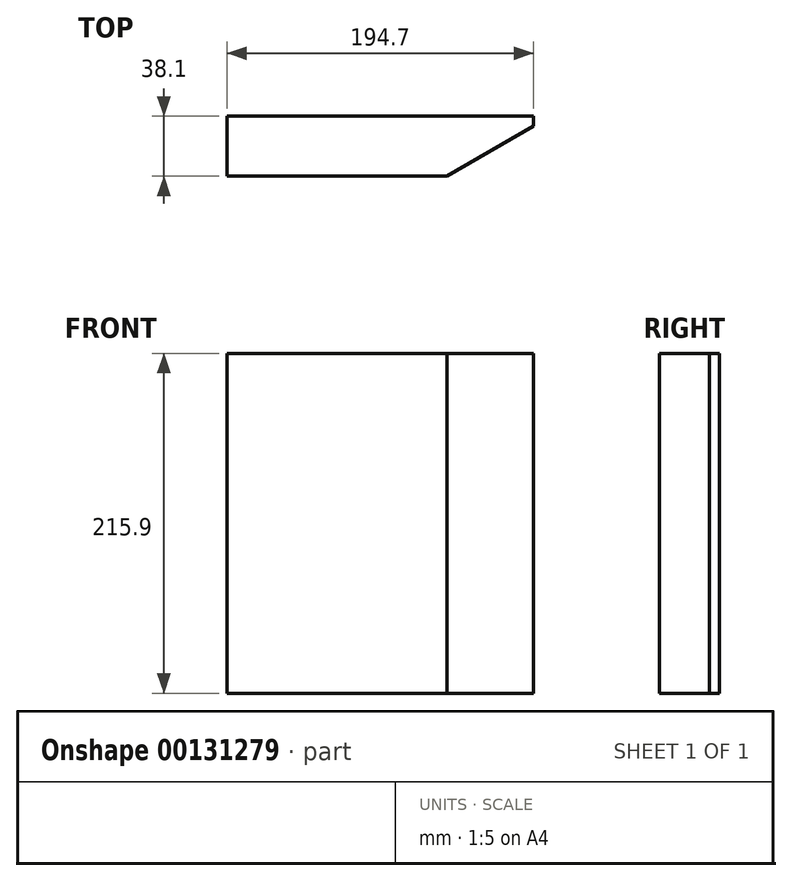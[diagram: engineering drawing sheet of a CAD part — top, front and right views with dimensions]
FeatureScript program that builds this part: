
annotation { "Feature Type Name" : "Feature", "Feature Type Description" : "" }
export const myFeature = defineFeature(function(context is Context, id is Id, definition is map)
    precondition{}
    {
        {
            var Q0;
            Q0=qCreatedBy(makeId("Top.planeOp"),FACE);
            var sketch = newSketch(context, id + "F0", { "sketchPlane" : qUnion([Q0])});
            skLineSegment(sketch, "E0.bottom", {"start": v(-91.69, -31.23) * mm, "end": v(116.1, -31.23) * mm});
            skLineSegment(sketch, "E0.top", {"start": v(-91.69, 6.87) * mm, "end": v(114, 6.87) * mm});
            skLineSegment(sketch, "E0.left", {"start": v(-91.69, -31.23) * mm, "end": v(-91.69, 6.87) * mm});
            skLineSegment(sketch, "E1", {"start": v(48.01, -31.23) * mm, "end": v(48.01, 6.87) * mm, "construction": true});
            skLineSegment(sketch, "E2", {"start": v(-91.69, 6.87) * mm, "end": v(-53.59, 6.87) * mm});
            skLineSegment(sketch, "E3", {"start": v(-91.69, -31.23) * mm, "end": v(48.01, -31.23) * mm});
            skLineSegment(sketch, "E4", {"start": v(48.01, -31.23) * mm, "end": v(114, 6.87) * mm});
            skLineSegment(sketch, "E5", {"start": v(103, 6.87) * mm, "end": v(103, 0.52) * mm});
            skSolve(sketch);
        }
        {
            var Q0;
            Q0=makeQuery(id+"F0.imprint","IMPRINT",FACE,{"disambiguationData":[TD([[makeQuery(id+"F0.imprint","IMPRINT",EDGE,{"derivedFrom":sQuery(id+"F0.wireOp",EDGE,"E0.left")}),-1.0]])]});
            var Q1;
            Q1=sQuery(id+"F0.wireOp",EDGE,"mc5OqN7e-pT2L-U8Of-l7ob-8pWatDAe0yvc");
            extrude(context, id + "F1", {"entities" : qUnion([Q0]), "surfaceEntities" : qUnion([Q1]), "depth" : 215.9 * mm});
        }
    });
